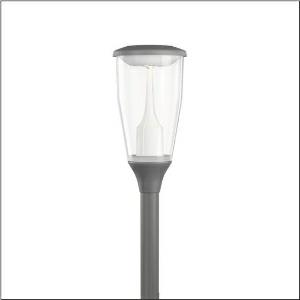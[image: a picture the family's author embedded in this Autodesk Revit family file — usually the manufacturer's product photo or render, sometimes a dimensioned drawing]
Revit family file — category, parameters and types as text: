
# Revit family: dl_11_iq___st1_2a_5xa5575ef14hp00022_53ae
name_source: partatom
category: Lighting Fixtures
units: mm (PartAtom-declared; Revit-internal decimal feet)

## family parameters
Cut with Voids When Loaded = No
Host = Face
Light Source = No
Part Type = Normal
Room Calculation Point = No
Round Connector Dimension = Use Diameter
Shared = No

## types (1)
- --- (1 x LED, 4840 lm, 33.6 W, 3000K)
    Apparent Load = 34 VA
    CIE Flux Codes = 23 60 93 95 100
    Color Rendering = 70
    Color Temperature = 3000K
    Default Elevation = 1800 mm
    Description = DL 11 iQ, mast luminaire, Module 540 iQ-SR, primary light control with 3 zone facetted reflector, of plastic, silver coated, highly specular, structured, primary optical cover: cover, of PMMA, transparent, light distribution: ST1.2a, light emission: direct distribution, primary light characteristic: asymmetric, installation type: post-top, LED, High Power LED, rated luminous flux: 4.840lm, luminous efficacy: 144lm/W, light colour: 730, colour temperature: 3000K, control gear: iQ Street-Remote, control: Street-Remote, Auto-Match, Temp-Guard, Lumen-Switch, Night-Set, Smart-Wire, Light-Fading, Desk-Remote (wireless, voltage-free reading and setting of iQ features in the workshop via application-optimized NFC function/RFID function), optimised constant luminous flux control (CLO 2.0), mains connection: 220..240V, AC, 50/60Hz, connection cable pre-assembled, cable length: 5,5m, start of lifetime: 34W, end of service life: 36W, reduction: 15W, luminaire housing, upper part, of diecast aluminium, coated, SITECO metallic grey (DB 702S), spigot size: 76mm (post-top), mounting height: 3..5m, post-top mast mounting element, of diecast aluminium, coated, SITECO metallic grey (DB 702S), Module 540 iQ-SR, traffic white (RAL 9016), equipment: Power, protection rating (complete): IP66, insulation class (complete): insulation class II (safety insulation), certification: CE, ENEC, ENEC+, VDE, impact resistance: IK07, packaging unit: 1 piece

Light Distribution: ST1.2a
    Height = 665 mm
    Lamp = 1 x LED
    Lamp Light Flux = 4840 lm
    Lamp Power = 33.6 W
    Lamp count = 1
    Length = 334 mm
    Luminous efficacy = 144 lm/W
    Manufacturer = Siteco
    ModVariant = No
    Model = 5XA5575EF14HP00022
    Number of Poles = 1
    OnlyDefault = Yes
    Power Factor = 1
    Product Name = DL 11 iQ | ST1.2a
    Product group = mast luminaire | pylon top
    ProductGroupID = 6100
    Protection Class = Protection class II
    Protection Degree = IP 66
    RLX_Detail_Level = 1
    RLX_Emergency_Light_Flux = 0 lm
    RLX_Emergency_Type = 0
    RLX_Emergency_Type_DB = No
    RlxData = <blob elided: 155145 chars, md5=1041c803>
    Socket = socket
    Standby Power = 0 W
    System Light Flux = 4840 lm
    System Power = 34 W
    Type Comments = factory setting: luminous flux: 100 % | dim-lin: 254 | 695 mA
    Type Image = l_1258354.jpg
    URL = http://relux.com
    VarID = @adj_040159
    Voltage = 0 V
    Weight = 0.00 kg
    Width = 0 mm  [stored 0 ft]

note: [stored X ft] marks values corroborated as IEEE doubles in the binary element streams (Revit-internal decimal feet)

## geometry (parser evidence)
native form markers: Blend x4, Sweep x10
no freeform markers — native parametric forms only
